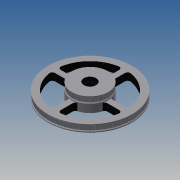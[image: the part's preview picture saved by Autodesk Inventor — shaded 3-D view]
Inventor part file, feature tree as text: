
AUTODESK INVENTOR PART (.ipt)
format: ipt  version: 2013 (Build 170138000, 138)  size: 1,558,016 bytes
history: native  units: mm
features: extrude x4, sketch x4, other x3, fillet x1, pattern_circular x1
ambient origin geometry x8: Origin, YZ Plane, XZ Plane, XY Plane, X Axis, Y Axis, Z Axis, Center Point
bodies: Solid1 (feature_tree)
feature tree (13):
  other  "z idler pulley.iam"
  other  "235 pulley blank.ipt:1"
  other  "100 pulley blank.ipt:1"
  extrude  "Extrusion1"  Depth=15.0mm
  extrude  "Extrusion2"  Depth=22.0mm
  extrude  "Extrusion3"  Depth=7.0mm TaperAngle=0.0deg
  extrude  "Extrusion4"  Depth=5.0mm
  fillet  "Fillet1"  Radius=12.0mm
  pattern_circular  "Circular Pattern1"  [2 undecoded]
  sketch  "Sketch1"  dims[d0=10.0mm d1=15.0mm]
  sketch  "Sketch2"  dims[d3=10.0mm d4=0.0mm d5=22.0mm]
  sketch  "Sketch3"  dims[d7=7.0mm d8=0.0mm d9=7.0mm d10=0.0mm]
  sketch  "Sketch4"  dims[d11=5.0mm d12=5.0mm d13=12.0mm d14=7.0mm d15=0.0mm d16=5.0mm d17=40.0mm d18=360.0deg]
note: 2 required parameter values undecoded (feature->parameter linkage not recoverable at this tier; creation-order binding heuristic only, values carry confidence <= 0.55)
